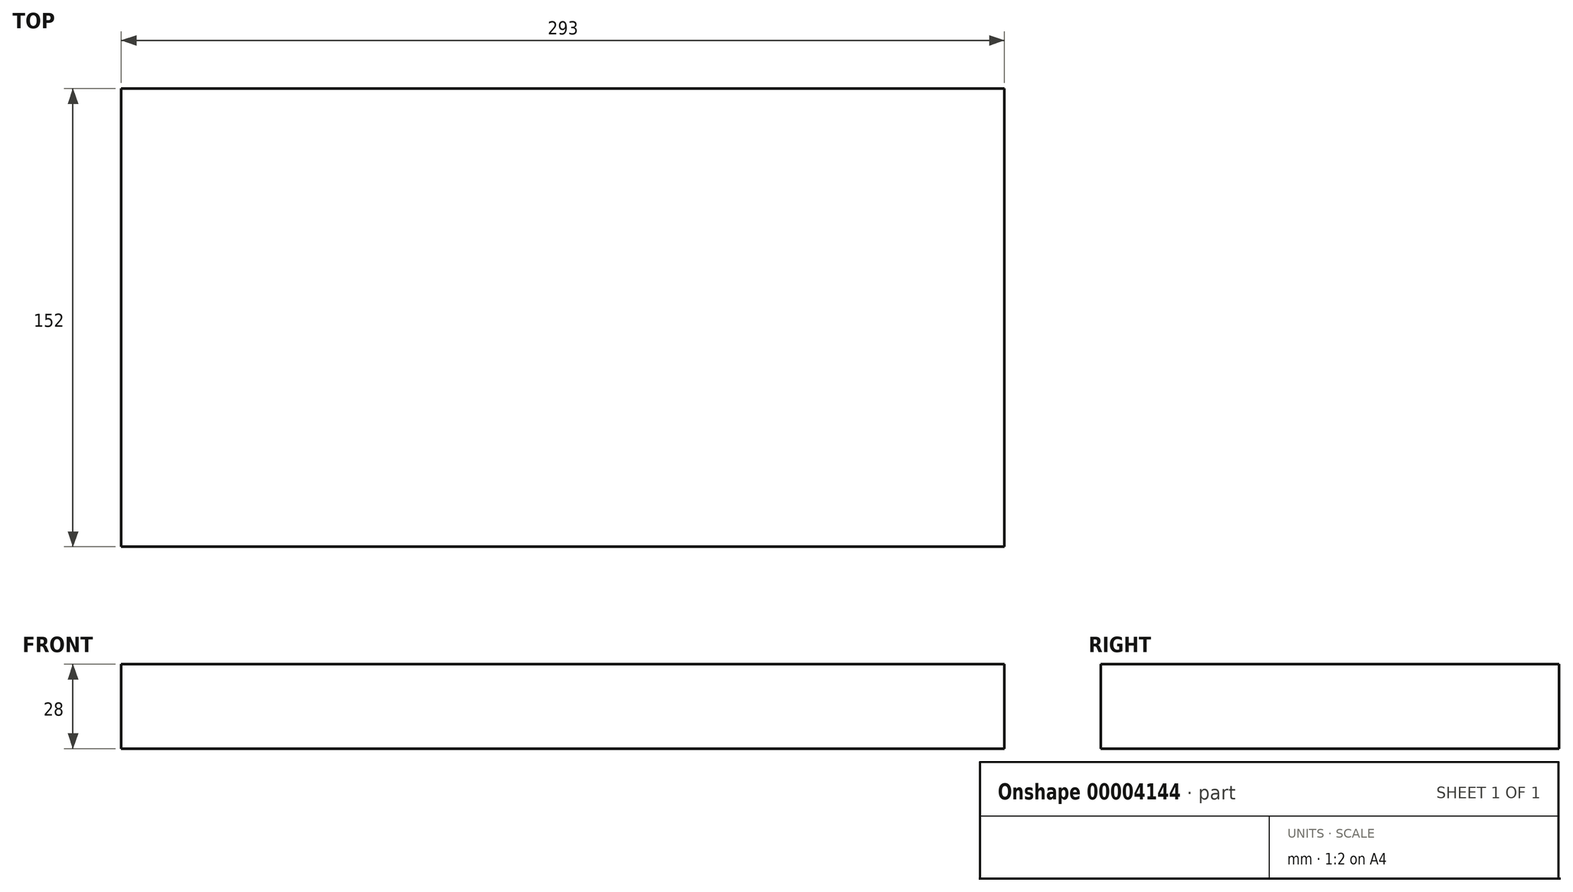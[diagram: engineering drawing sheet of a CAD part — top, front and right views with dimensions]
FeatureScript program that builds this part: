
annotation { "Feature Type Name" : "Feature", "Feature Type Description" : "" }
export const myFeature = defineFeature(function(context is Context, id is Id, definition is map)
    precondition{}
    {
        {
            var Q0;
            Q0=qCreatedBy(makeId("Top.planeOp"),FACE);
            var sketch = newSketch(context, id + "F0", { "sketchPlane" : qUnion([Q0])});
            skLineSegment(sketch, "E0.rect.bottom", {"start": v(146.5, -76) * mm, "end": v(-146.5, -76) * mm});
            skLineSegment(sketch, "E0.rect.top", {"start": v(146.5, 76) * mm, "end": v(-146.5, 76) * mm});
            skLineSegment(sketch, "E0.rect.left", {"start": v(146.5, -76) * mm, "end": v(146.5, 76) * mm});
            skLineSegment(sketch, "E0.rect.right", {"start": v(-146.5, -76) * mm, "end": v(-146.5, 76) * mm});
            skPoint(sketch, "E0.rect.middle", {"position": v(0, 0) * mm});
            skLineSegment(sketch, "E1", {"start": v(146.5, 76) * mm, "end": v(-146.5, -76) * mm, "construction": true});
            skLineSegment(sketch, "E2", {"start": v(-146.5, 76) * mm, "end": v(146.5, -76) * mm, "construction": true});
            skSolve(sketch);
        }
        {
            var Q0;
            Q0=makeQuery(id+"F0.imprint","IMPRINT",FACE,{"disambiguationData":[TD([[makeQuery(id+"F0.imprint","IMPRINT",EDGE,{"derivedFrom":sQuery(id+"F0.wireOp",EDGE,"E0.rect.bottom")}),-1.0]])]});
            extrude(context, id + "F1", {"entities" : qUnion([Q0]), "depth" : (56 / 2) * mm});
        }
    });
